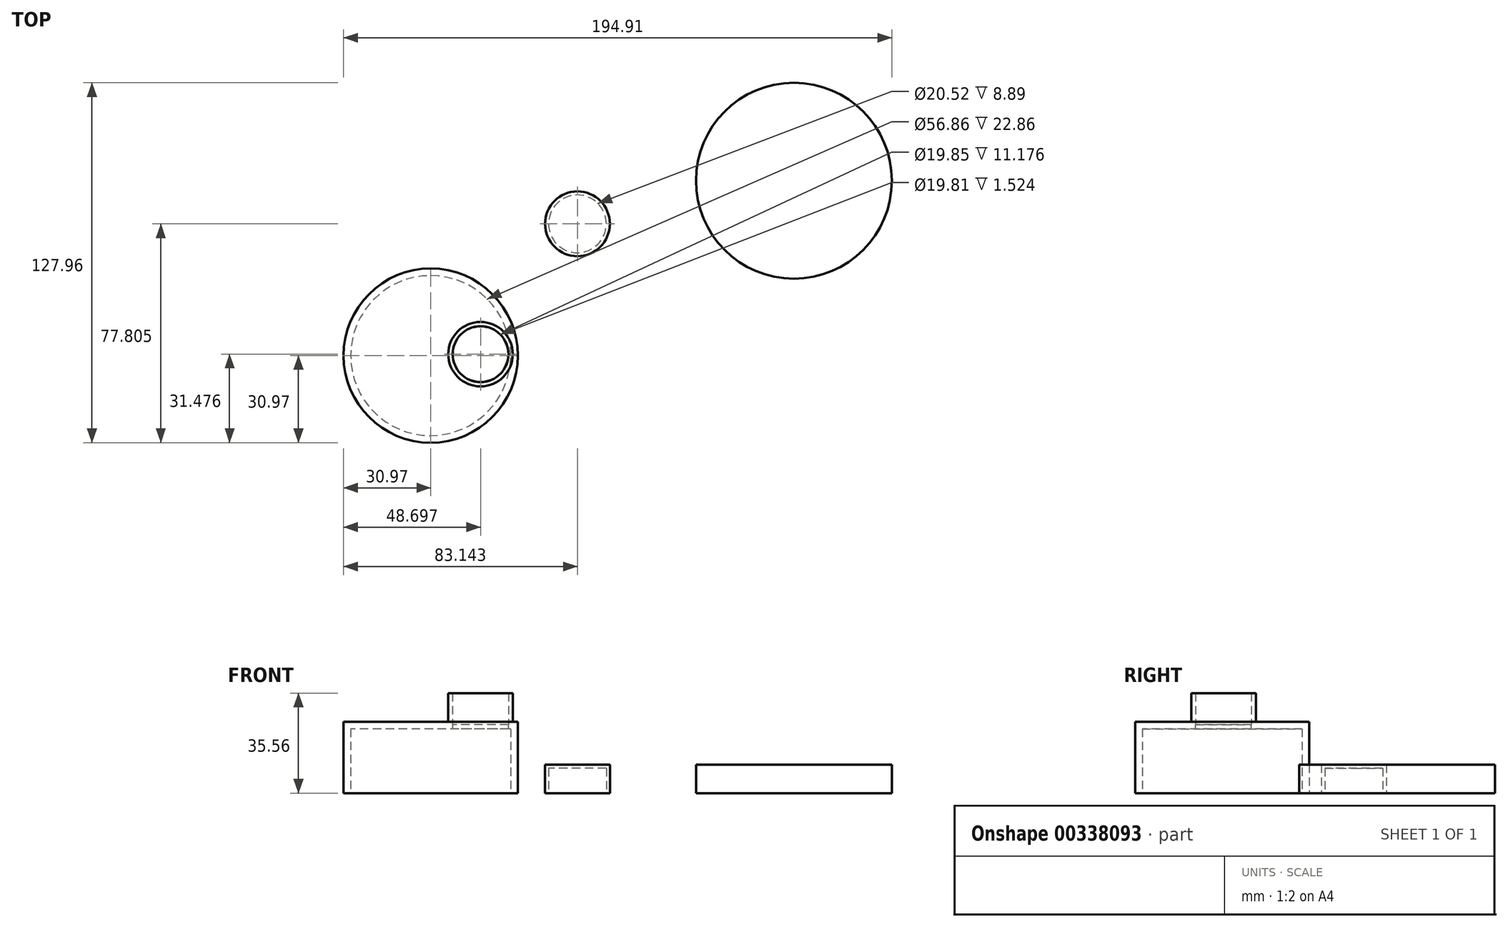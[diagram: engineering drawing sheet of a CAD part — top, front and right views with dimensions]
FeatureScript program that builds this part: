
annotation { "Feature Type Name" : "Feature", "Feature Type Description" : "" }
export const myFeature = defineFeature(function(context is Context, id is Id, definition is map)
    precondition{}
    {
        {
            var Q0;
            Q0=qCreatedBy(makeId("Top.planeOp"),FACE);
            var sketch = newSketch(context, id + "F0", { "sketchPlane" : qUnion([Q0])});
            skCircle(sketch, "E0", {"center": v(0, 0) * mm, "radius": 30.97 * mm});
            skSolve(sketch);
        }
        {
            var Q0;
            Q0=makeQuery(id+"F0.imprint","IMPRINT",FACE,{"disambiguationData":[TD([[makeQuery(id+"F0.imprint","IMPRINT",EDGE,{"derivedFrom":sQuery(id+"F0.wireOp",EDGE,"E0")}),1.0]])]});
            extrude(context, id + "F1", {"entities" : qUnion([Q0]), "depth" : 25.4 * mm});
        }
        {
            var Q0;
            Q0=makeQuery(id+"F1.opExtrude","CAP_FACE",FACE,{"disambiguationData":[OSD([sQuery(id+"F0.wireOp",EDGE,"E0")])],"isStart":true});
            shell(context, id + "F2", {"entities" : qUnion([Q0]), "thickness" : 2.54 * mm});
        }
        {
            var Q0;
            Q0=makeQuery(id+"F1.opExtrude","CAP_FACE",FACE,{"disambiguationData":[OSD([sQuery(id+"F0.wireOp",EDGE,"E0")])],"isStart":false});
            cPlane(context, id + "F3", {"entities" : qUnion([Q0]), "cplaneType" : CPlaneType.OFFSET, "offset" : 0 * mm, "width" : 152.4 * mm, "height" : 152.4 * mm});
        }
        {
            var Q0;
            Q0=qCreatedBy(id+"F3.planeOp",FACE);
            var sketch = newSketch(context, id + "F4", { "sketchPlane" : qUnion([Q0])});
            skCircle(sketch, "E1", {"center": v(17.73, 0.5) * mm, "radius": 11.45 * mm});
            skSolve(sketch);
        }
        {
            var Q0;
            Q0=makeQuery(id+"F4.imprint","IMPRINT",FACE,{"disambiguationData":[TD([[makeQuery(id+"F4.imprint","IMPRINT",EDGE,{"derivedFrom":sQuery(id+"F4.wireOp",EDGE,"E1")}),1.0]])]});
            extrude(context, id + "F5", {"entities" : qUnion([Q0]), "operationType" : NewBodyOperationType.ADD, "depth" : 10.16 * mm});
        }
        {
            var Q0;
            Q0=makeQuery(id+"F5.opExtrude","CAP_FACE",FACE,{"disambiguationData":[OSD([sQuery(id+"F4.wireOp",EDGE,"E1")])],"isStart":false});
            shell(context, id + "F6", {"entities" : qUnion([Q0]), "thickness" : 1.52 * mm});
        }
        {
            var Q0;
            Q0=makeQuery(id+"F6.opShell","OFFSET_FACE",FACE,{"disambiguationData":[OSD([sQuery(id+"F0.wireOp",EDGE,"E0")])]});
            var sketch = newSketch(context, id + "F7", { "sketchPlane" : qUnion([Q0])});
            skPoint(sketch, "E2", {"position": v(17.73, 0.5) * mm});
            skSolve(sketch);
        }
        {
            var Q0;
            Q0=sQuery(id+"F7.wireOp",VERTEX,"E2");
            var Q1;
            Q1=makeQuery(id+"F1.opExtrude","SWEPT_BODY",BODY,{"disambiguationData":[OSD([sQuery(id+"F0.wireOp",EDGE,"E0")])]});
            hole(context, id + "F8", {"style" : HoleStyle.SIMPLE, "endStyle" : HoleEndStyle.THROUGH, "holeDiameter" : 19.8 * mm, "tappedDepth" : 12.7 * mm, "tapClearance" : 3, "locations" : qUnion([Q0]), "scope" : qUnion([Q1])});
        }
        {
            var Q0;
            Q0=qCreatedBy(makeId("Top.planeOp"),FACE);
            var sketch = newSketch(context, id + "F9", { "sketchPlane" : qUnion([Q0])});
            skCircle(sketch, "E3", {"center": v(52.17, 46.84) * mm, "radius": 11.53 * mm});
            skCircle(sketch, "E4", {"center": v(129.12, 62.16) * mm, "radius": 34.82 * mm});
            skSolve(sketch);
        }
        {
            var Q0;
            Q0=makeQuery(id+"F9.imprint","IMPRINT",FACE,{"disambiguationData":[TD([[makeQuery(id+"F9.imprint","IMPRINT",EDGE,{"derivedFrom":sQuery(id+"F9.wireOp",EDGE,"E3")}),1.0]])]});
            var Q1;
            Q1 = qSketchRegion(id + "F9", true);
            extrude(context, id + "F10", {"entities" : qUnion([Q0, Q1]), "depth" : 10.16 * mm});
        }
        {
            var Q0;
            Q0=makeQuery(id+"F10.opExtrude","CAP_FACE",FACE,{"disambiguationData":[OSD([sQuery(id+"F9.wireOp",EDGE,"E3")])],"isStart":true});
            shell(context, id + "F11", {"entities" : qUnion([Q0]), "thickness" : 1.27 * mm});
        }
    });
